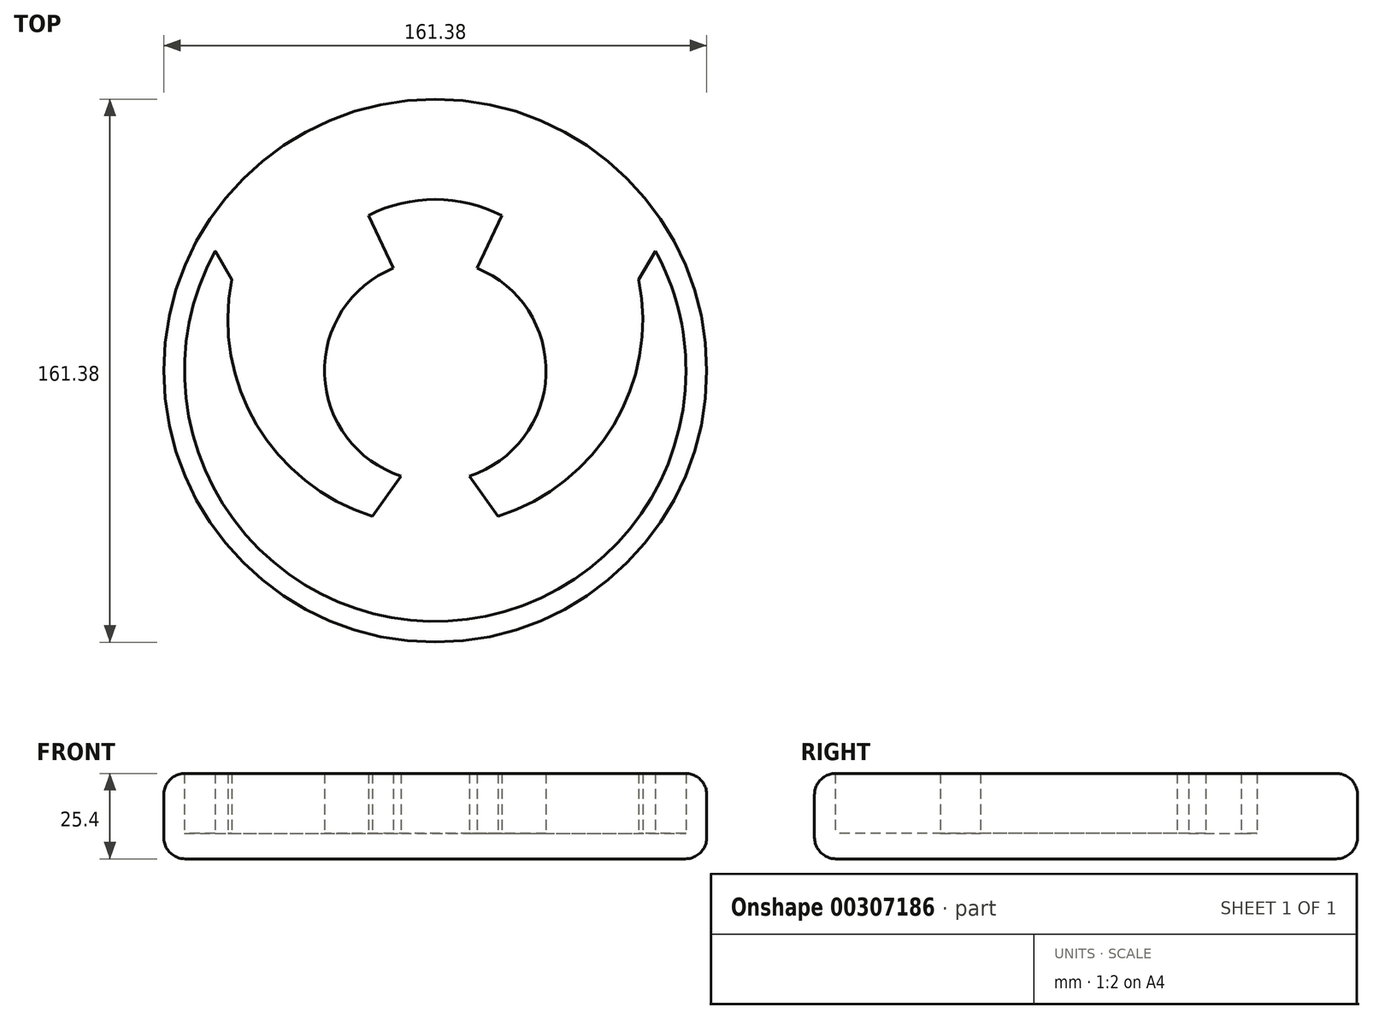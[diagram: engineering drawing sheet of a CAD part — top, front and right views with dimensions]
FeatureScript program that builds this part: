
annotation { "Feature Type Name" : "Feature", "Feature Type Description" : "" }
export const myFeature = defineFeature(function(context is Context, id is Id, definition is map)
    precondition{}
    {
        {
            var Q0;
            Q0=qCreatedBy(makeId("Top.planeOp"),FACE);
            var sketch = newSketch(context, id + "F0", { "sketchPlane" : qUnion([Q0])});
            skCircle(sketch, "E0", {"center": v(0, 0) * mm, "radius": 74.5 * mm});
            skCircle(sketch, "E1", {"center": v(0, 0) * mm, "radius": 32.91 * mm});
            skLineSegment(sketch, "E2", {"start": v(-65.45, 35.6) * mm, "end": v(-60.49, 27.1) * mm});
            skArc(sketch, "E3", {"start": v(-60.49, 27.1) * mm, "mid": v(-53.05, -16.08) * mm, "end": v(-18.67, -43.23) * mm});
            skArc(sketch, "E4.MirrorCS", {"start": v(60.49, 27.1) * mm, "mid": v(53.05, -16.08) * mm, "end": v(18.67, -43.23) * mm});
            skLineSegment(sketch, "E5.MirrorCS", {"start": v(65.45, 35.6) * mm, "end": v(60.49, 27.1) * mm});
            skLineSegment(sketch, "E6", {"start": v(-18.67, -43.23) * mm, "end": v(-10.2, -31.3) * mm});
            skLineSegment(sketch, "E7.MirrorCS", {"start": v(18.67, -43.23) * mm, "end": v(10.2, -31.3) * mm});
            skArc(sketch, "E8", {"start": v(31.34, 37.5) * mm, "mid": v(-0.84, 50.89) * mm, "end": v(-32.57, 36.46) * mm});
            skLineSegment(sketch, "E9", {"start": v(-12.42, 30.48) * mm, "end": v(-19.87, 46.17) * mm});
            skLineSegment(sketch, "E10.MirrorCS", {"start": v(12.42, 30.48) * mm, "end": v(19.87, 46.17) * mm});
            skCircle(sketch, "E11", {"center": v(0, 0) * mm, "radius": 80.69 * mm});
            skSolve(sketch);
        }
        {
            var Q0;
            Q0 = qSketchRegion(id + "F0", true);
            var Q1;
            {var subQ7=sQuery(id+"F0.wireOp",EDGE,"E2");Q1=makeQuery(id+"F0.imprint","IMPRINT",FACE,{"disambiguationData":[TD([[makeQuery(id+"F0.imprint","IMPRINT",EDGE,{"derivedFrom":subQ7}),1.0]])]});}
            extrude(context, id + "F1", {"entities" : qUnion([Q0, Q1]), "depth" : 25.4 * mm});
        }
        {
            var Q0;
            {var subQ0=sQuery(id+"F0.wireOp",EDGE,"E1");var subQ1=makeQuery(id+"F0.imprint","INTERSECT",VERTEX,{"derivedFrom":[subQ0,sQuery(id+"F0.wireOp",EDGE,"E9")]});Q0=makeQuery(id+"F0.imprint","IMPRINT",FACE,{"disambiguationData":[TD([[makeQuery(id+"F0.imprint","IMPRINT",EDGE,{"disambiguationData":[TD([[subQ1,1.0]])],"derivedFrom":subQ0}),1.0]])]});}
            var Q1;
            {var subQ0=sQuery(id+"F0.wireOp",EDGE,"E9");Q1=makeQuery(id+"F0.imprint","IMPRINT",FACE,{"disambiguationData":[TD([[makeQuery(id+"F0.imprint","IMPRINT",EDGE,{"derivedFrom":subQ0}),-1.0]])]});}
            var Q2;
            {var subQ3=sQuery(id+"F0.wireOp",EDGE,"E2");Q2=makeQuery(id+"F0.imprint","IMPRINT",FACE,{"disambiguationData":[TD([[makeQuery(id+"F0.imprint","IMPRINT",EDGE,{"derivedFrom":subQ3}),-1.0]])]});}
            extrude(context, id + "F2", {"entities" : qUnion([Q0, Q1, Q2]), "operationType" : NewBodyOperationType.ADD, "depth" : 7.62 * mm});
        }
        {
            var Q0;
            Q0=makeQuery(id+"F1.opExtrude","CAP_EDGE",EDGE,{"disambiguationData":[OSD([sQuery(id+"F0.wireOp",EDGE,"E11")])],"isStart":false});
            var Q1;
            Q1=makeQuery(id+"F1.opExtrude","CAP_EDGE",EDGE,{"disambiguationData":[OSD([sQuery(id+"F0.wireOp",EDGE,"E11")])],"isStart":true});
            fillet(context, id + "F3", {"entities" : qUnion([Q0, Q1]), "radius" : 6.35 * mm, "tangentPropagation" : true, "allowEdgeOverflow" : false});
        }
    });
